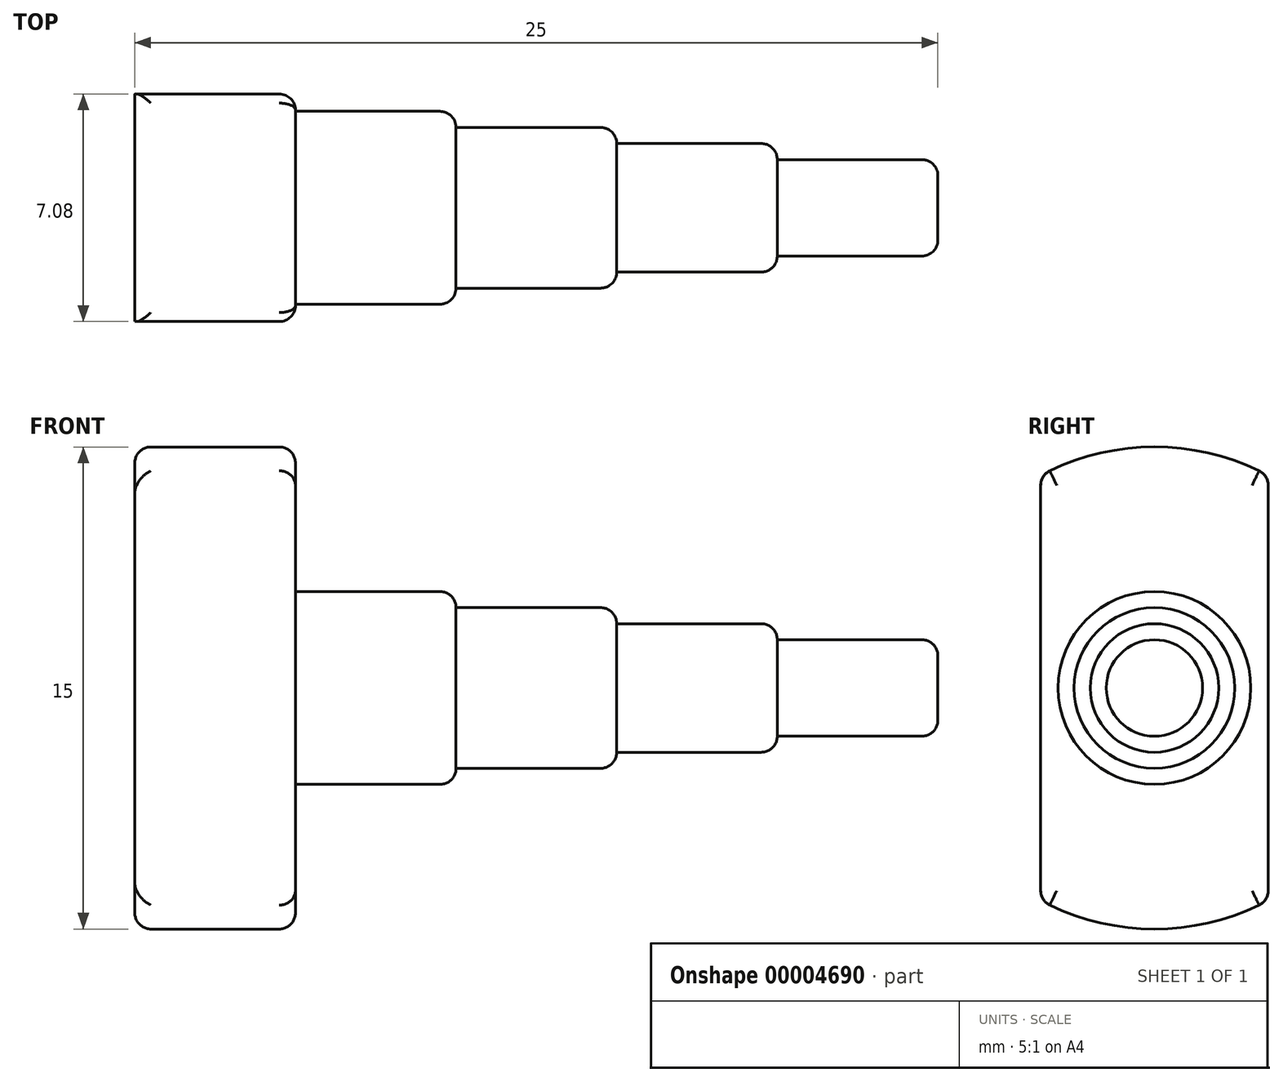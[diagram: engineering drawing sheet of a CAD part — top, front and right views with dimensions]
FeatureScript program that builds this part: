
annotation { "Feature Type Name" : "Feature", "Feature Type Description" : "" }
export const myFeature = defineFeature(function(context is Context, id is Id, definition is map)
    precondition{}
    {
        {
            var Q0;
            Q0=qCreatedBy(makeId("Top.planeOp"),FACE);
            var sketch = newSketch(context, id + "F0", { "sketchPlane" : qUnion([Q0])});
            skLineSegment(sketch, "E0.bottom", {"start": v(0, 0) * mm, "end": v(5, 0) * mm});
            skLineSegment(sketch, "E0.top", {"start": v(0, -3) * mm, "end": v(5, -3) * mm});
            skLineSegment(sketch, "E0.left", {"start": v(0, 0) * mm, "end": v(0, -3) * mm});
            skLineSegment(sketch, "E0.right", {"start": v(5, 0) * mm, "end": v(5, -3) * mm});
            skLineSegment(sketch, "E1.bottom", {"start": v(5, 0) * mm, "end": v(10, 0) * mm});
            skLineSegment(sketch, "E1.top", {"start": v(5, -2.5) * mm, "end": v(10, -2.5) * mm});
            skLineSegment(sketch, "E1.left", {"start": v(5, 0) * mm, "end": v(5, -2.5) * mm});
            skLineSegment(sketch, "E1.right", {"start": v(10, 0) * mm, "end": v(10, -2.5) * mm});
            skLineSegment(sketch, "E2.bottom", {"start": v(10, 0) * mm, "end": v(15, 0) * mm});
            skLineSegment(sketch, "E2.top", {"start": v(10, -2) * mm, "end": v(15, -2) * mm});
            skLineSegment(sketch, "E2.left", {"start": v(10, 0) * mm, "end": v(10, -2) * mm});
            skLineSegment(sketch, "E2.right", {"start": v(15, 0) * mm, "end": v(15, -2) * mm});
            skLineSegment(sketch, "E3.bottom", {"start": v(15, 0) * mm, "end": v(20, 0) * mm});
            skLineSegment(sketch, "E3.top", {"start": v(15, -1.5) * mm, "end": v(20, -1.5) * mm});
            skLineSegment(sketch, "E3.left", {"start": v(15, 0) * mm, "end": v(15, -1.5) * mm});
            skLineSegment(sketch, "E3.right", {"start": v(20, 0) * mm, "end": v(20, -1.5) * mm});
            skLineSegment(sketch, "E4.bottom", {"start": v(0, 0) * mm, "end": v(-5, 0) * mm});
            skLineSegment(sketch, "E4.top", {"start": v(0, -7.5) * mm, "end": v(-5, -7.5) * mm});
            skLineSegment(sketch, "E4.left", {"start": v(0, 0) * mm, "end": v(0, -7.5) * mm});
            skLineSegment(sketch, "E4.right", {"start": v(-5, 0) * mm, "end": v(-5, -7.5) * mm});
            skSolve(sketch);
        }
        {
            var Q0;
            Q0=makeQuery(id+"F0.imprint","IMPRINT",FACE,{"disambiguationData":[TD([[makeQuery(id+"F0.imprint","IMPRINT",EDGE,{"derivedFrom":sQuery(id+"F0.wireOp",EDGE,"E3.bottom")}),-1.0]])]});
            var Q1;
            Q1=makeQuery(id+"F0.imprint","IMPRINT",FACE,{"disambiguationData":[TD([[makeQuery(id+"F0.imprint","IMPRINT",EDGE,{"derivedFrom":sQuery(id+"F0.wireOp",EDGE,"E1.bottom")}),-1.0]])]});
            var Q2;
            Q2=makeQuery(id+"F0.imprint","IMPRINT",FACE,{"disambiguationData":[TD([[makeQuery(id+"F0.imprint","IMPRINT",EDGE,{"derivedFrom":sQuery(id+"F0.wireOp",EDGE,"E2.bottom")}),-1.0]])]});
            var Q3;
            {var subQ2=sQuery(id+"F0.wireOp",EDGE,"E0.bottom");Q3=makeQuery(id+"F0.imprint","IMPRINT",FACE,{"disambiguationData":[TD([[makeQuery(id+"F0.imprint","IMPRINT",EDGE,{"derivedFrom":subQ2}),-1.0]])]});}
            var Q4;
            {var subQ3=sQuery(id+"F0.wireOp",EDGE,"E4.bottom");Q4=makeQuery(id+"F0.imprint","IMPRINT",FACE,{"disambiguationData":[TD([[makeQuery(id+"F0.imprint","IMPRINT",EDGE,{"derivedFrom":subQ3}),1.0]])]});}
            var Q5;
            Q5=sQuery(id+"F0.wireOp",EDGE,"E4.bottom");
            revolve(context, id + "F1", {"entities" : qUnion([Q0, Q1, Q2, Q3, Q4]), "axis" : qUnion([Q5]), "revolveType" : RevolveType.FULL});
        }
        {
            var Q0;
            Q0=makeQuery(id+"F1.opRevolve","SWEPT_EDGE",EDGE,{"disambiguationData":[OSD([sQuery(id+"F0.wireOp",EDGE,"E3.top"),sQuery(id+"F0.wireOp",EDGE,"E3.right")])]});
            var Q1;
            Q1=makeQuery(id+"F1.opRevolve","SWEPT_EDGE",EDGE,{"disambiguationData":[OSD([sQuery(id+"F0.wireOp",EDGE,"E2.top"),sQuery(id+"F0.wireOp",EDGE,"E2.right")])]});
            var Q2;
            Q2=makeQuery(id+"F1.opRevolve","SWEPT_EDGE",EDGE,{"disambiguationData":[OSD([sQuery(id+"F0.wireOp",EDGE,"E1.top"),sQuery(id+"F0.wireOp",EDGE,"E1.right")])]});
            var Q3;
            Q3=makeQuery(id+"F1.opRevolve","SWEPT_EDGE",EDGE,{"disambiguationData":[OSD([sQuery(id+"F0.wireOp",EDGE,"E0.top"),sQuery(id+"F0.wireOp",EDGE,"E0.right")])]});
            var Q4;
            Q4=makeQuery(id+"F1.opRevolve","SWEPT_EDGE",EDGE,{"disambiguationData":[OSD([sQuery(id+"F0.wireOp",EDGE,"E4.top"),sQuery(id+"F0.wireOp",EDGE,"E4.left")])]});
            fillet(context, id + "F2", {"entities" : qUnion([Q0, Q1, Q2, Q3, Q4]), "radius" : 0.5 * mm, "tangentPropagation" : true, "allowEdgeOverflow" : false});
        }
        {
            var Q0;
            Q0=makeQuery(id+"F1.opRevolve","SWEPT_FACE",FACE,{"disambiguationData":[OSD([sQuery(id+"F0.wireOp",EDGE,"E4.right")])]});
            var sketch = newSketch(context, id + "F3", { "sketchPlane" : qUnion([Q0])});
            skLineSegment(sketch, "E5.bottom", {"start": v(3.54, 8.3) * mm, "end": v(8.39, 8.3) * mm});
            skLineSegment(sketch, "E5.top", {"start": v(3.54, -8.3) * mm, "end": v(8.39, -8.3) * mm});
            skLineSegment(sketch, "E5.left", {"start": v(3.54, 8.3) * mm, "end": v(3.54, -8.3) * mm});
            skLineSegment(sketch, "E5.right", {"start": v(8.39, 8.3) * mm, "end": v(8.39, -8.3) * mm});
            skLineSegment(sketch, "E6.bottom", {"start": v(-3.54, 8.3) * mm, "end": v(-8.39, 8.3) * mm});
            skLineSegment(sketch, "E6.top", {"start": v(-3.54, -8.3) * mm, "end": v(-8.39, -8.3) * mm});
            skLineSegment(sketch, "E6.left", {"start": v(-3.54, 8.3) * mm, "end": v(-3.54, -8.3) * mm});
            skLineSegment(sketch, "E6.right", {"start": v(-8.39, 8.3) * mm, "end": v(-8.39, -8.3) * mm});
            skLineSegment(sketch, "E7", {"start": v(8.39, 0) * mm, "end": v(3.54, 0) * mm, "construction": true});
            skLineSegment(sketch, "E8", {"start": v(3.54, 0) * mm, "end": v(-3.54, 0) * mm, "construction": true});
            skLineSegment(sketch, "E9", {"start": v(-3.54, 0) * mm, "end": v(-8.39, 0) * mm, "construction": true});
            skSolve(sketch);
        }
        {
            var Q0;
            Q0 = qSketchRegion(id + "F3", true);
            extrude(context, id + "F4", {"entities" : qUnion([Q0]), "operationType" : NewBodyOperationType.REMOVE, "oppositeDirection" : true, "depth" : 25 * mm});
        }
        {
            var Q0;
            Q0=makeQuery(id+"F4.boolean.opBoolean","INTERSECT",EDGE,{"disambiguationData":[OD(1.0)],"derivedFrom":[makeQuery(id+"F1.opRevolve","SWEPT_FACE",FACE,{"disambiguationData":[OSD([sQuery(id+"F0.wireOp",EDGE,"E4.top")])]}),makeQuery(id+"F4.opExtrude","SWEPT_FACE",FACE,{"disambiguationData":[OSD([sQuery(id+"F3.wireOp",EDGE,"E5.left")])]})]});
            var Q1;
            Q1=makeQuery(id+"F4.boolean.opBoolean","INTERSECT",EDGE,{"disambiguationData":[OD(0.0)],"derivedFrom":[makeQuery(id+"F1.opRevolve","SWEPT_FACE",FACE,{"disambiguationData":[OSD([sQuery(id+"F0.wireOp",EDGE,"E4.top")])]}),makeQuery(id+"F4.opExtrude","SWEPT_FACE",FACE,{"disambiguationData":[OSD([sQuery(id+"F3.wireOp",EDGE,"E6.left")])]})]});
            var Q2;
            Q2=makeQuery(id+"F4.boolean.opBoolean","COPY",EDGE,{"derivedFrom":makeQuery(id+"F4.opExtrude","CAP_EDGE",EDGE,{"disambiguationData":[OSD([sQuery(id+"F3.wireOp",EDGE,"E6.left")])],"isStart":true})});
            var Q3;
            Q3=makeQuery(id+"F4.boolean.opBoolean","SPLIT",EDGE,{"disambiguationData":[OD(1.0)],"derivedFrom":makeQuery(id+"F1.opRevolve","SWEPT_EDGE",EDGE,{"disambiguationData":[OSD([sQuery(id+"F0.wireOp",EDGE,"E4.top"),sQuery(id+"F0.wireOp",EDGE,"E4.right")])]})});
            var Q4;
            Q4=makeQuery(id+"F4.boolean.opBoolean","SPLIT",EDGE,{"disambiguationData":[OD(0.0)],"derivedFrom":makeQuery(id+"F1.opRevolve","SWEPT_EDGE",EDGE,{"disambiguationData":[OSD([sQuery(id+"F0.wireOp",EDGE,"E4.top"),sQuery(id+"F0.wireOp",EDGE,"E4.right")])]})});
            var Q5;
            Q5=makeQuery(id+"F4.boolean.opBoolean","COPY",EDGE,{"derivedFrom":makeQuery(id+"F4.opExtrude","CAP_EDGE",EDGE,{"disambiguationData":[OSD([sQuery(id+"F3.wireOp",EDGE,"E5.left")])],"isStart":true})});
            fillet(context, id + "F5", {"entities" : qUnion([Q0, Q1, Q2, Q3, Q4, Q5]), "radius" : 0.5 * mm, "tangentPropagation" : true, "allowEdgeOverflow" : false});
        }
    });
